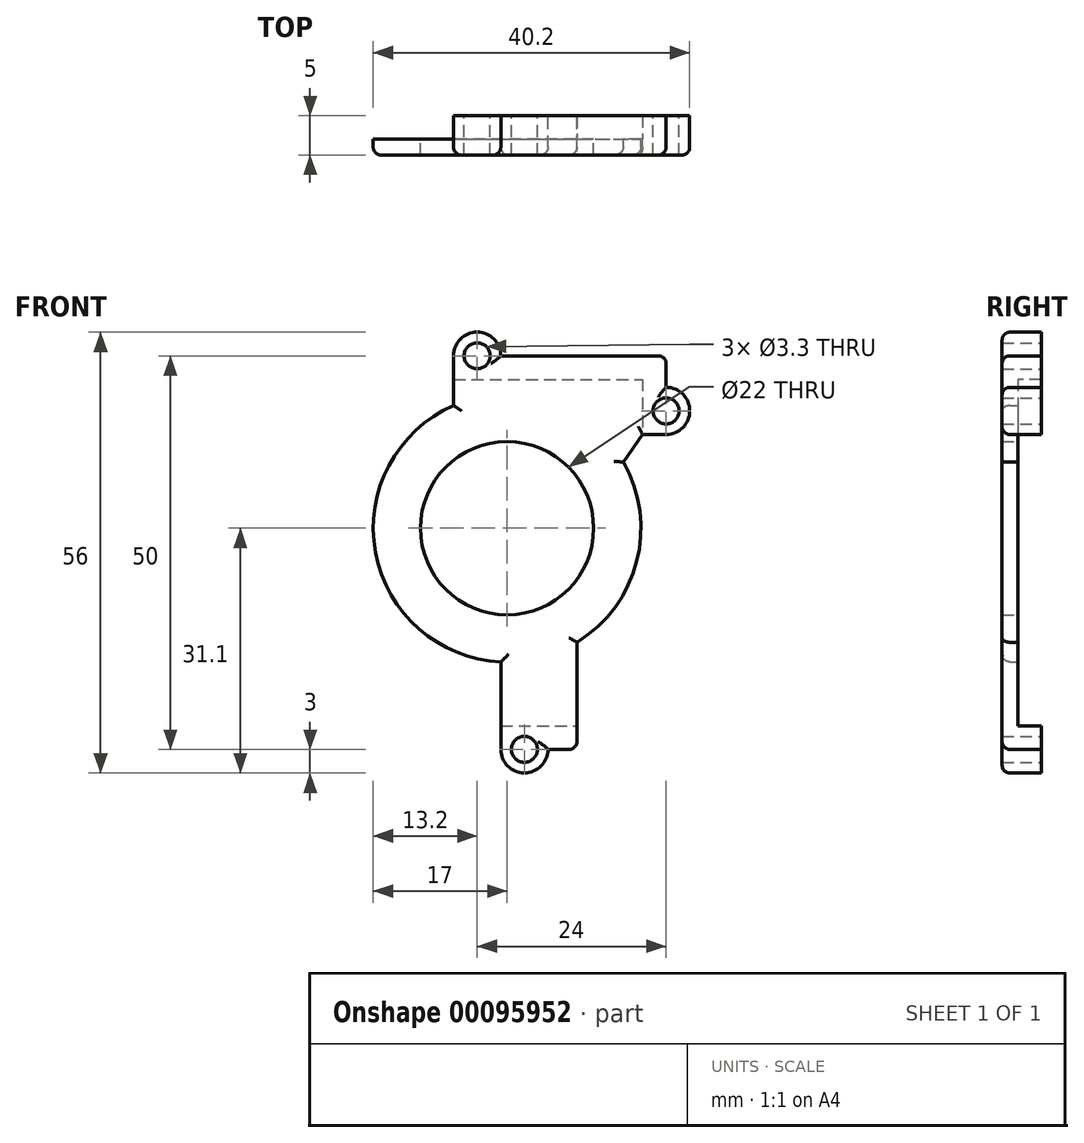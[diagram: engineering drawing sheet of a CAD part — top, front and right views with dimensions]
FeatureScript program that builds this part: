
annotation { "Feature Type Name" : "Feature", "Feature Type Description" : "" }
export const myFeature = defineFeature(function(context is Context, id is Id, definition is map)
    precondition{}
    {
        {
            var Q0;
            Q0=qCreatedBy(makeId("Front.planeOp"),FACE);
            var sketch = newSketch(context, id + "F0", { "sketchPlane" : qUnion([Q0])});
            skLineSegment(sketch, "E0.bottom", {"start": v(38, 44) * mm, "end": v(62, 44) * mm});
            skLineSegment(sketch, "E0.top", {"start": v(44, 0) * mm, "end": v(62, 0) * mm});
            skLineSegment(sketch, "E0.right", {"start": v(62, 44) * mm, "end": v(62, 0) * mm});
            skLineSegment(sketch, "E1.bottom", {"start": v(38, 47) * mm, "end": v(65, 47) * mm});
            skLineSegment(sketch, "E1.top", {"start": v(44, -3) * mm, "end": v(65, -3) * mm});
            skLineSegment(sketch, "E1.right", {"start": v(65, 47) * mm, "end": v(65, -3) * mm});
            skArc(sketch, "E2", {"start": v(44, 47) * mm, "mid": v(41, 50) * mm, "end": v(38, 47) * mm});
            skArc(sketch, "E3", {"start": v(65, 37) * mm, "mid": v(68, 40) * mm, "end": v(65, 43) * mm});
            skArc(sketch, "E4", {"start": v(44, -3) * mm, "mid": v(47, -6) * mm, "end": v(50, -3) * mm});
            skCircle(sketch, "E5", {"center": v(41, 47) * mm, "radius": 1.65 * mm});
            skCircle(sketch, "E6", {"center": v(65, 40) * mm, "radius": 1.65 * mm});
            skCircle(sketch, "E7", {"center": v(47, -3) * mm, "radius": 1.65 * mm});
            skCircle(sketch, "E8", {"center": v(44.8, 25.1) * mm, "radius": 11 * mm});
            skLineSegment(sketch, "E9", {"start": v(38, 47) * mm, "end": v(38, 40.68) * mm});
            skLineSegment(sketch, "E10", {"start": v(44, -3) * mm, "end": v(44, 8.12) * mm});
            skArc(sketch, "E11", {"start": v(38, 40.68) * mm, "mid": v(28.08, 22.02) * mm, "end": v(44, 8.12) * mm});
            skCircle(sketch, "E12", {"center": v(44.8, 25.1) * mm, "radius": 17 * mm, "construction": true});
            skLineSegment(sketch, "E13", {"start": v(65, 37) * mm, "end": v(62, 37) * mm});
            skLineSegment(sketch, "E14", {"start": v(62, 37) * mm, "end": v(59.57, 33.52) * mm});
            skLineSegment(sketch, "E15", {"start": v(53.69, -3) * mm, "end": v(53.69, 10.6) * mm});
            skArc(sketch, "E16", {"start": v(53.69, 10.6) * mm, "mid": v(61.27, 20.87) * mm, "end": v(59.57, 33.52) * mm});
            skSolve(sketch);
        }
        {
            var Q0;
            {var subQ14=sQuery(id+"F0.wireOp",EDGE,"E0.bottom");Q0=makeQuery(id+"F0.imprint","IMPRINT",FACE,{"disambiguationData":[TD([[makeQuery(id+"F0.imprint","IMPRINT",EDGE,{"derivedFrom":subQ14}),1.0]])]});}
            var Q1;
            {var subQ0=sQuery(id+"F0.wireOp",EDGE,"E2");Q1=makeQuery(id+"F0.imprint","IMPRINT",FACE,{"disambiguationData":[TD([[makeQuery(id+"F0.imprint","IMPRINT",EDGE,{"derivedFrom":subQ0}),1.0]])]});}
            var Q2;
            {var subQ7=sQuery(id+"F0.wireOp",EDGE,"E0.bottom");Q2=makeQuery(id+"F0.imprint","IMPRINT",FACE,{"disambiguationData":[TD([[makeQuery(id+"F0.imprint","IMPRINT",EDGE,{"derivedFrom":subQ7}),-1.0]])]});}
            var Q3;
            {var subQ5=sQuery(id+"F0.wireOp",EDGE,"E0.top");var subQ9=sQuery(id+"F0.wireOp",EDGE,"E10");var subQ12=makeQuery(id+"F0.imprint","INTERSECT",VERTEX,{"derivedFrom":[subQ5,subQ9]});Q3=makeQuery(id+"F0.imprint","IMPRINT",FACE,{"disambiguationData":[TD([[makeQuery(id+"F0.imprint","IMPRINT",EDGE,{"disambiguationData":[TD([[subQ12,-1.0]])],"derivedFrom":subQ5}),-1.0]])]});}
            var Q4;
            {var subQ0=sQuery(id+"F0.wireOp",EDGE,"E4");Q4=makeQuery(id+"F0.imprint","IMPRINT",FACE,{"disambiguationData":[TD([[makeQuery(id+"F0.imprint","IMPRINT",EDGE,{"derivedFrom":subQ0}),1.0]])]});}
            var Q5;
            {var subQ0=sQuery(id+"F0.wireOp",EDGE,"E3");Q5=makeQuery(id+"F0.imprint","IMPRINT",FACE,{"disambiguationData":[TD([[makeQuery(id+"F0.imprint","IMPRINT",EDGE,{"derivedFrom":subQ0}),1.0]])]});}
            extrude(context, id + "F1", {"entities" : qUnion([Q0, Q1, Q2, Q3, Q4, Q5]), "depth" : 2 * mm});
        }
        {
            var Q0;
            {var subQ0=sQuery(id+"F0.wireOp",EDGE,"E2");Q0=makeQuery(id+"F0.imprint","IMPRINT",FACE,{"disambiguationData":[TD([[makeQuery(id+"F0.imprint","IMPRINT",EDGE,{"derivedFrom":subQ0}),1.0]])]});}
            var Q1;
            {var subQ11=sQuery(id+"F0.wireOp",EDGE,"E0.bottom");Q1=makeQuery(id+"F0.imprint","IMPRINT",FACE,{"disambiguationData":[TD([[makeQuery(id+"F0.imprint","IMPRINT",EDGE,{"derivedFrom":subQ11}),1.0]])]});}
            var Q2;
            {var subQ0=sQuery(id+"F0.wireOp",EDGE,"E3");Q2=makeQuery(id+"F0.imprint","IMPRINT",FACE,{"disambiguationData":[TD([[makeQuery(id+"F0.imprint","IMPRINT",EDGE,{"derivedFrom":subQ0}),1.0]])]});}
            var Q3;
            {var subQ0=sQuery(id+"F0.wireOp",EDGE,"E4");Q3=makeQuery(id+"F0.imprint","IMPRINT",FACE,{"disambiguationData":[TD([[makeQuery(id+"F0.imprint","IMPRINT",EDGE,{"derivedFrom":subQ0}),1.0]])]});}
            var Q4;
            {var subQ5=sQuery(id+"F0.wireOp",EDGE,"E0.top");var subQ9=sQuery(id+"F0.wireOp",EDGE,"E10");var subQ12=makeQuery(id+"F0.imprint","INTERSECT",VERTEX,{"derivedFrom":[subQ5,subQ9]});Q4=makeQuery(id+"F0.imprint","IMPRINT",FACE,{"disambiguationData":[TD([[makeQuery(id+"F0.imprint","IMPRINT",EDGE,{"disambiguationData":[TD([[subQ12,-1.0]])],"derivedFrom":subQ5}),-1.0]])]});}
            extrude(context, id + "F2", {"entities" : qUnion([Q0, Q1, Q2, Q3, Q4]), "operationType" : NewBodyOperationType.ADD, "oppositeDirection" : true, "depth" : 3 * mm});
        }
        {
            var Q0;
            Q0=makeQuery(id+"F1.opExtrude","CAP_EDGE",EDGE,{"disambiguationData":[OSD([sQuery(id+"F0.wireOp",EDGE,"E9")])],"isStart":false});
            var Q1;
            Q1=makeQuery(id+"F1.opExtrude","CAP_EDGE",EDGE,{"disambiguationData":[OSD([sQuery(id+"F0.wireOp",EDGE,"E2")])],"isStart":false});
            var Q2;
            Q2=makeQuery(id+"F1.opExtrude","CAP_EDGE",EDGE,{"disambiguationData":[OSD([sQuery(id+"F0.wireOp",EDGE,"E1.bottom")])],"isStart":false});
            var Q3;
            Q3=makeQuery(id+"F1.opExtrude","CAP_EDGE",EDGE,{"disambiguationData":[OSD([sQuery(id+"F0.wireOp",EDGE,"E1.right")])],"isStart":false});
            var Q4;
            Q4=makeQuery(id+"F1.opExtrude","CAP_EDGE",EDGE,{"disambiguationData":[OSD([sQuery(id+"F0.wireOp",EDGE,"E3")])],"isStart":false});
            var Q5;
            Q5=makeQuery(id+"F1.opExtrude","CAP_EDGE",EDGE,{"disambiguationData":[OSD([sQuery(id+"F0.wireOp",EDGE,"E13")])],"isStart":false});
            var Q6;
            Q6=makeQuery(id+"F1.opExtrude","CAP_EDGE",EDGE,{"disambiguationData":[OSD([sQuery(id+"F0.wireOp",EDGE,"E14")])],"isStart":false});
            var Q7;
            Q7=makeQuery(id+"F1.opExtrude","CAP_EDGE",EDGE,{"disambiguationData":[OSD([sQuery(id+"F0.wireOp",EDGE,"E16")])],"isStart":false});
            var Q8;
            Q8=makeQuery(id+"F1.opExtrude","CAP_EDGE",EDGE,{"disambiguationData":[OSD([sQuery(id+"F0.wireOp",EDGE,"E10")])],"isStart":false});
            var Q9;
            Q9=makeQuery(id+"F1.opExtrude","CAP_EDGE",EDGE,{"disambiguationData":[OSD([sQuery(id+"F0.wireOp",EDGE,"E4")])],"isStart":false});
            var Q10;
            Q10=makeQuery(id+"F1.opExtrude","CAP_EDGE",EDGE,{"disambiguationData":[OSD([sQuery(id+"F0.wireOp",EDGE,"E1.top")])],"isStart":false});
            var Q11;
            Q11=makeQuery(id+"F1.opExtrude","CAP_EDGE",EDGE,{"disambiguationData":[OSD([sQuery(id+"F0.wireOp",EDGE,"E15")])],"isStart":false});
            var Q12;
            {var subQ0=sQuery(id+"F0.wireOp",EDGE,"E1.right");var subQ1=sQuery(id+"F0.wireOp",EDGE,"E1.bottom");Q12=makeQuery(id+"F2.boolean.opBoolean","MERGE",EDGE,{"derivedFrom":[makeQuery(id+"F1.opExtrude","SWEPT_EDGE",EDGE,{"disambiguationData":[OSD([subQ1,subQ0])]}),makeQuery(id+"F2.opExtrude","SWEPT_EDGE",EDGE,{"disambiguationData":[OSD([subQ1,subQ0])]})]});}
            var Q13;
            Q13=makeQuery(id+"F1.opExtrude","SWEPT_EDGE",EDGE,{"disambiguationData":[OSD([sQuery(id+"F0.wireOp",EDGE,"E1.top"),sQuery(id+"F0.wireOp",EDGE,"E15")])]});
            var Q14;
            Q14=makeQuery(id+"F1.opExtrude","CAP_EDGE",EDGE,{"disambiguationData":[OSD([sQuery(id+"F0.wireOp",EDGE,"E11")])],"isStart":false});
            fillet(context, id + "F3", {"entities" : qUnion([Q0, Q1, Q2, Q3, Q4, Q5, Q6, Q7, Q8, Q9, Q10, Q11, Q12, Q13, Q14]), "radius" : 1 * mm, "tangentPropagation" : true, "allowEdgeOverflow" : false});
        }
    });
